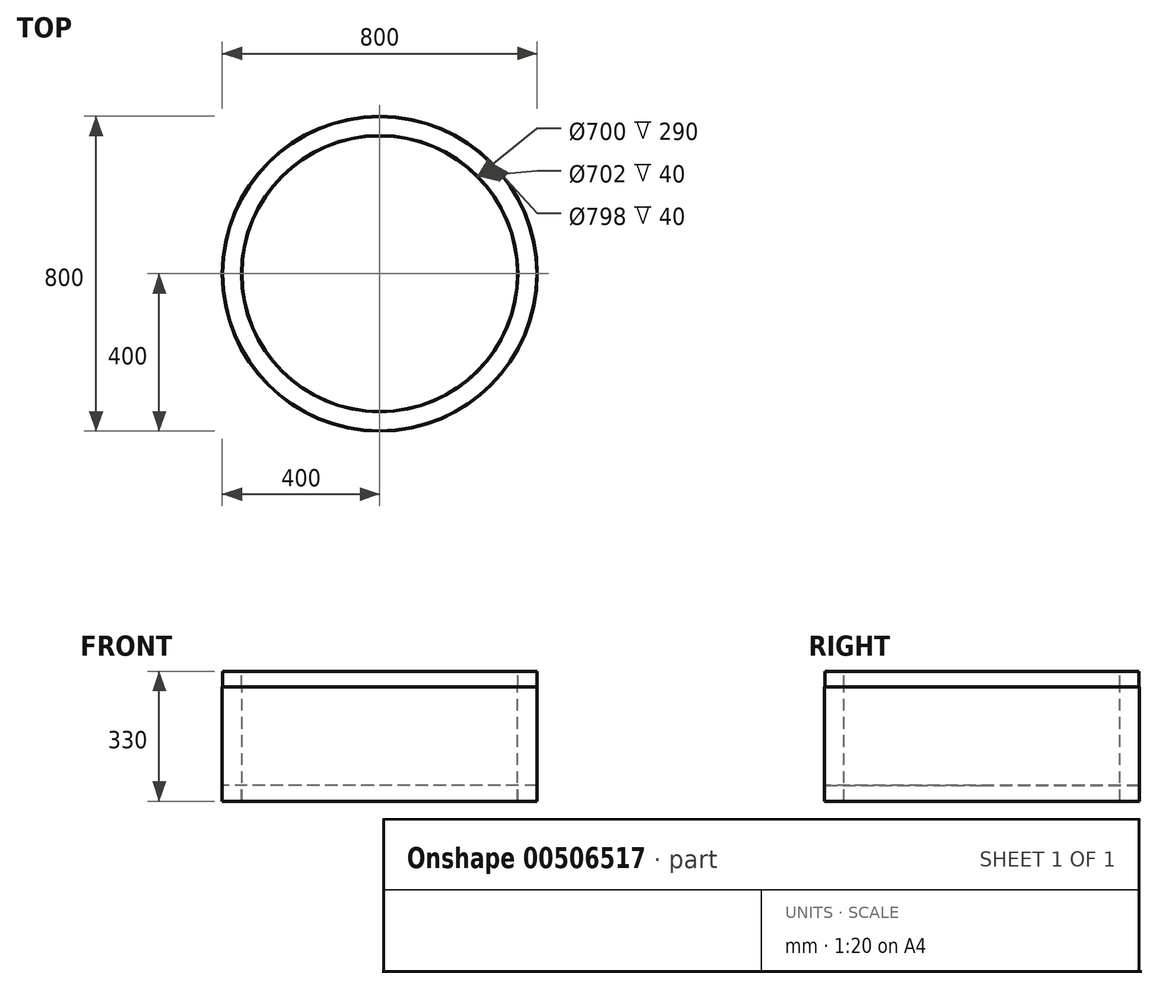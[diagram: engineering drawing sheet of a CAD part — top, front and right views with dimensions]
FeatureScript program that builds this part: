
annotation { "Feature Type Name" : "Feature", "Feature Type Description" : "" }
export const myFeature = defineFeature(function(context is Context, id is Id, definition is map)
    precondition{}
    {
        {
            var Q0;
            Q0=qCreatedBy(makeId("Front.planeOp"),FACE);
            var sketch = newSketch(context, id + "F0", { "sketchPlane" : qUnion([Q0])});
            skLineSegment(sketch, "E0", {"start": v(0, 74.87) * mm, "end": v(0, -73.71) * mm, "construction": true});
            skLineSegment(sketch, "E1", {"start": v(0, 374.84) * mm, "end": v(0, -528.94) * mm, "construction": true});
            skLineSegment(sketch, "E2", {"start": v(-350, -489.75) * mm, "end": v(-350, -199.75) * mm});
            skLineSegment(sketch, "E3", {"start": v(-350, -199.75) * mm, "end": v(-351, -199.75) * mm});
            skLineSegment(sketch, "E4", {"start": v(-351, -199.75) * mm, "end": v(-351, -159.75) * mm});
            skLineSegment(sketch, "E5", {"start": v(-351, -159.75) * mm, "end": v(-399, -159.75) * mm});
            skLineSegment(sketch, "E6", {"start": v(-399, -159.75) * mm, "end": v(-399, -199.75) * mm});
            skLineSegment(sketch, "E7", {"start": v(-399, -199.75) * mm, "end": v(-400, -199.75) * mm});
            skLineSegment(sketch, "E8", {"start": v(-400, -199.75) * mm, "end": v(-400, -489.75) * mm});
            skLineSegment(sketch, "E9", {"start": v(-400, -489.75) * mm, "end": v(-399, -489.75) * mm});
            skLineSegment(sketch, "E10", {"start": v(-399, -489.75) * mm, "end": v(-399, -449.75) * mm});
            skLineSegment(sketch, "E11", {"start": v(-399, -449.75) * mm, "end": v(-351, -449.75) * mm});
            skLineSegment(sketch, "E12", {"start": v(-351, -449.75) * mm, "end": v(-351, -489.75) * mm});
            skLineSegment(sketch, "E13", {"start": v(-351, -489.75) * mm, "end": v(-350, -489.75) * mm});
            skSolve(sketch);
        }
        {
            var Q0;
            Q0=qSketchRegion(id+"F0",true);
            var Q1;
            Q1=sQuery(id+"F0.wireOp",EDGE,"E1");
            revolve(context, id + "F1", {"entities" : qUnion([Q0]), "axis" : qUnion([Q1]), "revolveType" : RevolveType.FULL});
        }
    });
